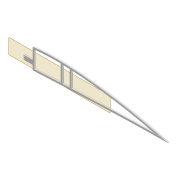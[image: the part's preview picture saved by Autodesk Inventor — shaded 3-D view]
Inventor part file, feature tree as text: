
AUTODESK INVENTOR PART (.ipt)
format: ipt  version: 2022 (Build 260153000, 153)  size: 432,640 bytes
history: native  units: mm
features: extrude x9, sketch x7, projected_geometry x6, fillet x2, shell x1, plane x1
ambient origin geometry x8: Origin, YZ Plane, XZ Plane, XY Plane, X Axis, Y Axis, Z Axis, Center Point
bodies: Solid1 (feature_tree)
feature tree (26):
  extrude  "Extrusion1"  Depth=5.0mm
  shell  "Shell1"  Thickness=2.0mm
  extrude  "Extrusion8"  Depth=5.9mm
  extrude  "Extrusion3"  Depth=10.0mm TaperAngle=0.0deg
  extrude  "Extrusion4"  Depth=2.0mm
  fillet  "Fillet1"  Radius=5.0mm
  sketch  "Sketch10"  dims[d22=4.0mm d23=0.0mm d31=2.0mm d32=5.0mm]
  extrude  "Extrusion5"  Depth=2.5mm
  plane  "Work Plane2"
  extrude  "Extrusion9"  Depth=1.6mm
  extrude  "Extrusion10"  Depth=0.5mm
  fillet  "Fillet2"  Radius=6.0mm
  extrude  "Extrusion11"  Depth=0.5mm TaperAngle=0.0deg
  extrude  "Extrusion12"  Depth=0.5mm
  sketch  "Sketch3"  dims[d0=4.0mm d1=0.0mm d2=5.0mm d7=2.0mm]
  sketch  "Sketch8"  dims[d8=2.0mm d9=5.9mm]
  sketch  "Sketch9"  dims[d13=10.0mm d14=0.0mm d16=10.0mm d17=0.0mm]
  projected_geometry  "Projected Loop4"
  projected_geometry  "Projected Loop10"
  sketch  "Sketch24"  dims[d34=1.6mm d35=2.5mm]
  projected_geometry  "Projected Loop11"
  projected_geometry  "Projected Loop12"
  projected_geometry  "Projected Loop13"
  sketch  "Sketch26"  dims[d37=5.0mm d38=1.6mm]
  projected_geometry  "Projected Loop14"
  sketch  "Sketch27"  dims[d40=2.5mm d62=80.0mm d63=6.0mm d64=4.0mm d65=0.0mm d66=3.0mm d67=12.0mm d68=5.0mm d69=25.0mm d70=12.0mm d71=3.05mm d72=4.0mm d73=0.0mm d74=10.0mm d75=0.0mm d76=2.0mm d77=100.0mm d78=20.0mm d79=0.5mm d80=10.0mm d81=0.0mm d82=10.0mm d83=0.0mm]
